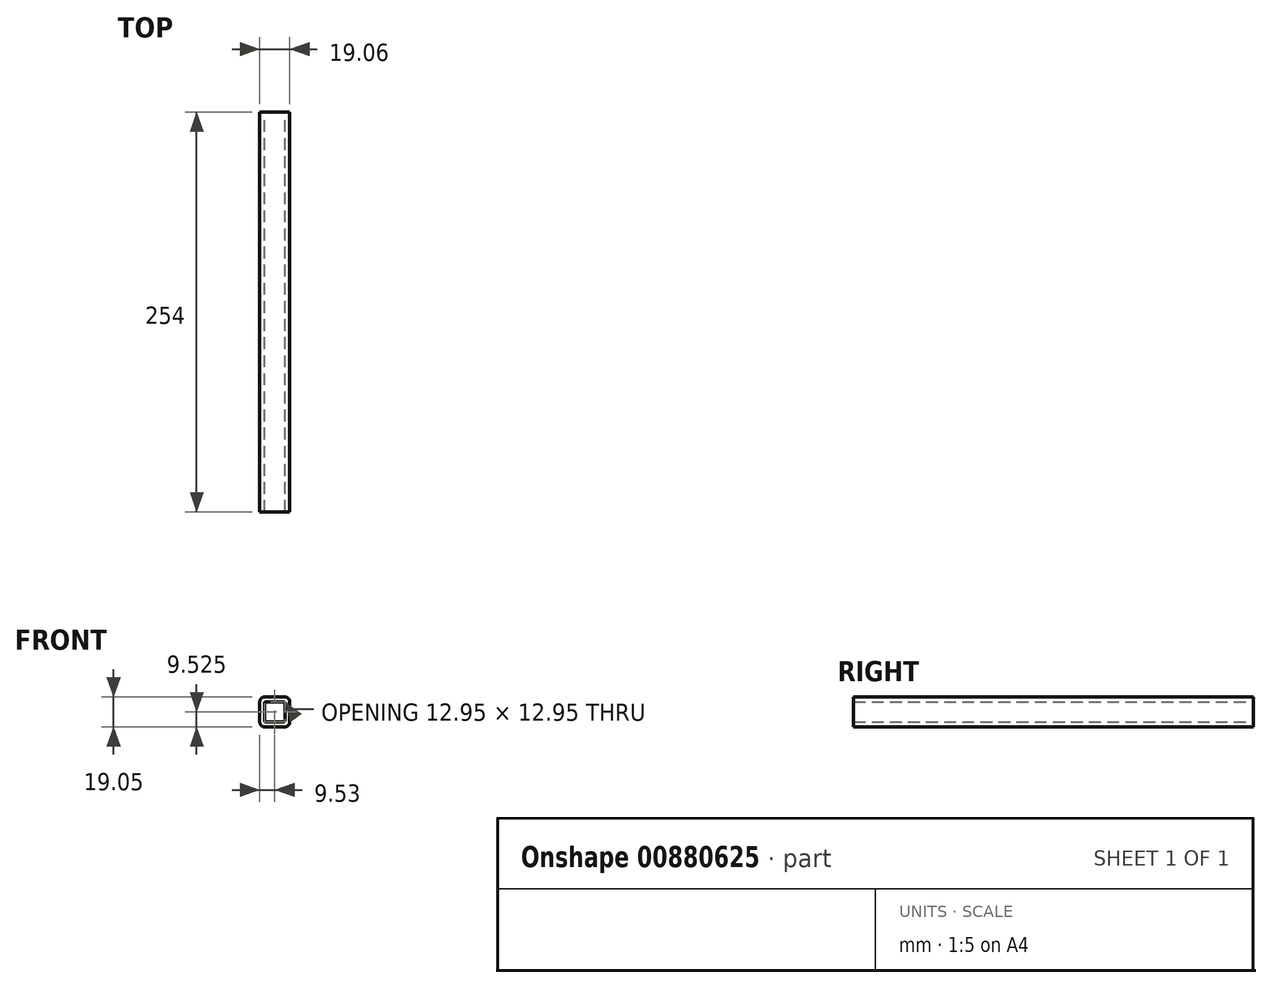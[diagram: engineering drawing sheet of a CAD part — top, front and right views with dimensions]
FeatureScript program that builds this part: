
annotation { "Feature Type Name" : "Feature", "Feature Type Description" : "" }
export const myFeature = defineFeature(function(context is Context, id is Id, definition is map)
    precondition{}
    {
        {
            var Q0;
            Q0=qCreatedBy(makeId("Front.planeOp"),FACE);
            var sketch = newSketch(context, id + "F0", { "sketchPlane" : qUnion([Q0])});
            skLineSegment(sketch, "E0.bottom", {"start": v(-6.35, 0) * mm, "end": v(6.35, 0) * mm});
            skLineSegment(sketch, "E0.top", {"start": v(-6.35, -19.05) * mm, "end": v(6.35, -19.05) * mm});
            skLineSegment(sketch, "E0.left", {"start": v(-9.52, -3.18) * mm, "end": v(-9.52, -15.88) * mm});
            skLineSegment(sketch, "E0.right", {"start": v(9.53, -3.17) * mm, "end": v(9.53, -15.88) * mm});
            skLineSegment(sketch, "E1.0", {"start": v(-5.46, -3.05) * mm, "end": v(5.46, -3.05) * mm});
            skLineSegment(sketch, "E1.1", {"start": v(-6.48, -4.06) * mm, "end": v(-6.48, -14.99) * mm});
            skLineSegment(sketch, "E1.2", {"start": v(-5.46, -16) * mm, "end": v(5.46, -16) * mm});
            skLineSegment(sketch, "E1.3", {"start": v(6.48, -4.06) * mm, "end": v(6.48, -14.99) * mm});
            skPoint(sketch, "E2.visualSharp", {"position": v(-9.53, 0) * mm});
            skArc(sketch, "E2.filletArc", {"start": v(-6.35, 0) * mm, "mid": v(-8.6, -0.93) * mm, "end": v(-9.52, -3.18) * mm});
            skPoint(sketch, "E3.visualSharp", {"position": v(-9.52, -19.05) * mm});
            skArc(sketch, "E3.filletArc", {"start": v(-9.52, -15.88) * mm, "mid": v(-8.6, -18.12) * mm, "end": v(-6.35, -19.05) * mm});
            skPoint(sketch, "E4.visualSharp", {"position": v(9.53, -19.05) * mm});
            skArc(sketch, "E4.filletArc", {"start": v(6.35, -19.05) * mm, "mid": v(8.6, -18.12) * mm, "end": v(9.52, -15.88) * mm});
            skPoint(sketch, "E5.visualSharp", {"position": v(9.53, 0) * mm});
            skArc(sketch, "E5.filletArc", {"start": v(9.53, -3.17) * mm, "mid": v(8.6, -0.93) * mm, "end": v(6.35, 0) * mm});
            skPoint(sketch, "E6.visualSharp", {"position": v(-6.48, -16) * mm});
            skArc(sketch, "E6.filletArc", {"start": v(-6.48, -14.99) * mm, "mid": v(-6.18, -15.7) * mm, "end": v(-5.46, -16) * mm});
            skPoint(sketch, "E7.visualSharp", {"position": v(6.48, -3.05) * mm});
            skArc(sketch, "E7.filletArc", {"start": v(6.48, -4.06) * mm, "mid": v(6.18, -3.35) * mm, "end": v(5.46, -3.05) * mm});
            skPoint(sketch, "E8.visualSharp", {"position": v(6.48, -16) * mm});
            skArc(sketch, "E8.filletArc", {"start": v(5.46, -16) * mm, "mid": v(6.18, -15.7) * mm, "end": v(6.48, -14.99) * mm});
            skPoint(sketch, "E9.visualSharp", {"position": v(-6.48, -3.05) * mm});
            skArc(sketch, "E9.filletArc", {"start": v(-5.46, -3.05) * mm, "mid": v(-6.18, -3.35) * mm, "end": v(-6.48, -4.06) * mm});
            skSolve(sketch);
        }
        {
            var Q0;
            Q0=makeQuery(id+"F0.imprint","IMPRINT",FACE,{"disambiguationData":[TD([[makeQuery(id+"F0.imprint","IMPRINT",EDGE,{"derivedFrom":sQuery(id+"F0.wireOp",EDGE,"E0.bottom")}),-1.0]])]});
            extrude(context, id + "F1", {"entities" : qUnion([Q0]), "depth" : 254 * mm, "offsetDistance" : 25.4 * mm});
        }
    });
